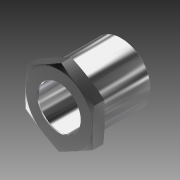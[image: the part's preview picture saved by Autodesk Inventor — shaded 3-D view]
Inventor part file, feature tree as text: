
AUTODESK INVENTOR PART (.ipt)
format: ipt  version: 2014 (Build 180170000, 170)  size: 152,064 bytes
history: native  units: mm (DEFAULTED — no unit token found)
features: sketch x4, plane x2, extrude x2, chamfer x1, revolve x1, reference x1
ambient origin geometry x8: Origin, YZ Plane, XZ Plane, XY Plane, X Axis, Y Axis, Z Axis, Center Point
bodies: Solid1 (feature_tree)
feature tree (11):
  sketch  "Sketch1"  dims[d2=7.9375mm d3=9.525mm d4=0.0mm]
  plane  "Work Plane1"
  extrude  "Extrusion1"  Depth=9.525mm TaperAngle=0.0deg
  extrude  "Extrusion2"  Depth=2.286mm TaperAngle=0.0deg
  chamfer  "Chamfer1"  Distance=0.127mm
  plane  "Work Plane2"
  revolve  "Revolution1"  [1 undecoded]
  sketch  "Sketch2"  dims[d5=12.7mm d6=2.286mm d7=0.0mm d8=0.127mm d9=0.127mm]
  reference  "Reference1"
  sketch  "Sketch3"  dims[d10=-6.35mm d11=1.745329mm]
  sketch  "Sketch4"  dims[d12=2.286mm d13=1.745329mm d14=2.286mm d15=3.96875mm d16=90.0deg d17=45.0deg]
note: 1 required parameter value undecoded (feature->parameter linkage not recoverable at this tier; creation-order binding heuristic only, values carry confidence <= 0.55)
